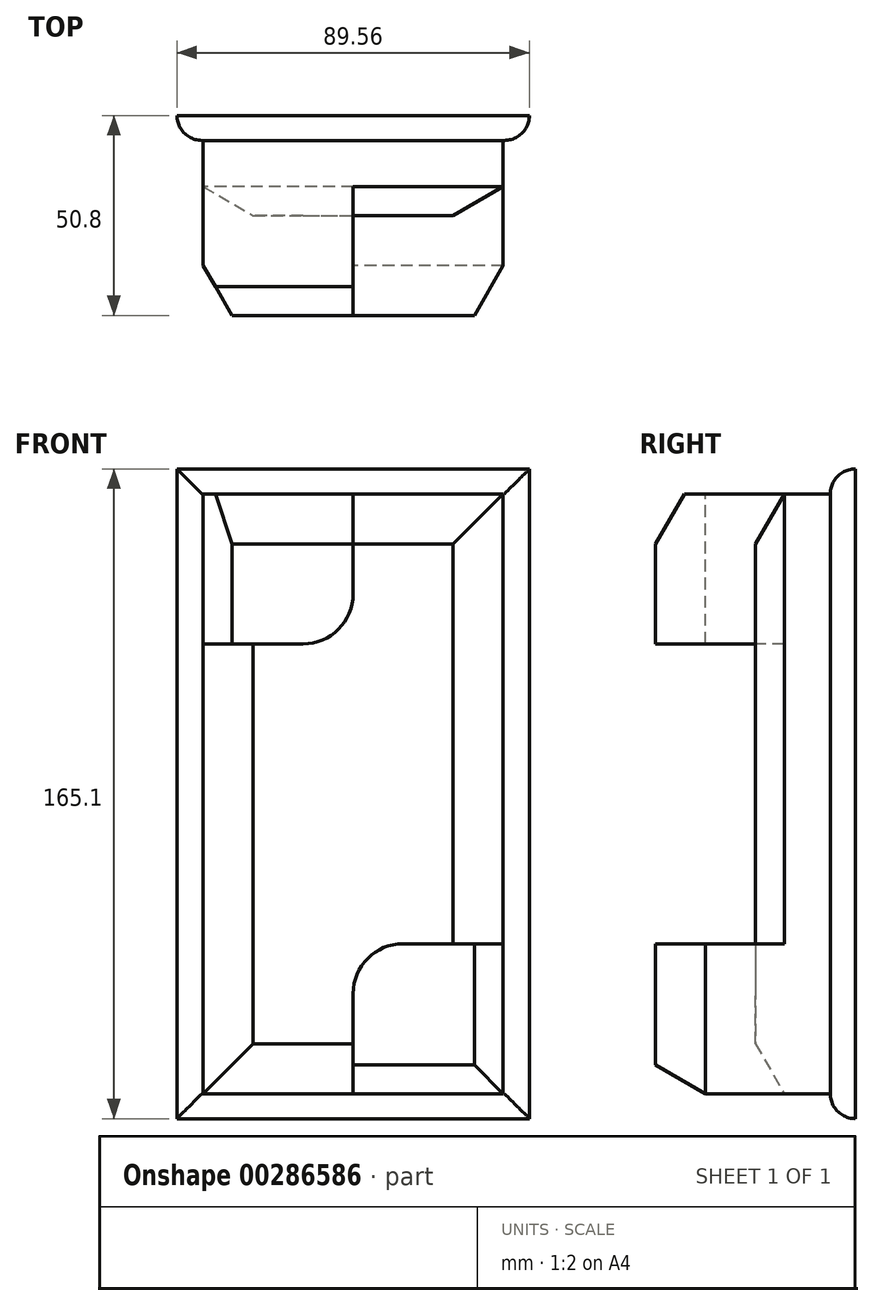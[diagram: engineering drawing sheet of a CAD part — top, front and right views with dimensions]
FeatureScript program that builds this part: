
annotation { "Feature Type Name" : "Feature", "Feature Type Description" : "" }
export const myFeature = defineFeature(function(context is Context, id is Id, definition is map)
    precondition{}
    {
        {
            var Q0;
            Q0=qCreatedBy(makeId("Front.planeOp"),FACE);
            var sketch = newSketch(context, id + "F0", { "sketchPlane" : qUnion([Q0])});
            skLineSegment(sketch, "E0.bottom", {"start": v(-44.78, 82.55) * mm, "end": v(44.78, 82.55) * mm});
            skLineSegment(sketch, "E0.top", {"start": v(-44.78, -82.55) * mm, "end": v(44.78, -82.55) * mm});
            skLineSegment(sketch, "E0.left", {"start": v(-44.78, 82.55) * mm, "end": v(-44.78, -82.55) * mm});
            skLineSegment(sketch, "E0.right", {"start": v(44.78, 82.55) * mm, "end": v(44.78, -82.55) * mm});
            skPoint(sketch, "E0.middle", {"position": v(0, 0) * mm});
            skLineSegment(sketch, "E1.bottom", {"start": v(-38.1, 76.2) * mm, "end": v(38.1, 76.2) * mm});
            skLineSegment(sketch, "E1.top", {"start": v(-38.1, -76.2) * mm, "end": v(38.1, -76.2) * mm});
            skLineSegment(sketch, "E1.left", {"start": v(-38.1, 76.2) * mm, "end": v(-38.1, -76.2) * mm});
            skLineSegment(sketch, "E1.right", {"start": v(38.1, 76.2) * mm, "end": v(38.1, -76.2) * mm});
            skLineSegment(sketch, "E2", {"start": v(0, 76.2) * mm, "end": v(0, 50.8) * mm});
            skPoint(sketch, "E2.endSnap0", {"position": v(0, 76.2) * mm});
            skLineSegment(sketch, "E3", {"start": v(-12.7, 38.1) * mm, "end": v(-38.1, 38.1) * mm});
            skLineSegment(sketch, "E4", {"start": v(0, -76.2) * mm, "end": v(0, -50.8) * mm});
            skPoint(sketch, "E4.endSnap0", {"position": v(0, -76.2) * mm});
            skLineSegment(sketch, "E5", {"start": v(12.7, -38.1) * mm, "end": v(38.1, -38.1) * mm});
            skArc(sketch, "E6", {"start": v(12.7, -38.1) * mm, "mid": v(3.72, -41.82) * mm, "end": v(0, -50.8) * mm});
            skArc(sketch, "E7", {"start": v(-12.7, 38.1) * mm, "mid": v(-3.72, 41.82) * mm, "end": v(0, 50.8) * mm});
            skPoint(sketch, "E8.orphan", {"position": v(0, 38.1) * mm});
            skPoint(sketch, "E9.orphan", {"position": v(0, -38.1) * mm});
            skSolve(sketch);
        }
        {
            var Q0;
            Q0=makeQuery(id+"F0.imprint","IMPRINT",FACE,{"disambiguationData":[TD([[makeQuery(id+"F0.imprint","IMPRINT",EDGE,{"derivedFrom":sQuery(id+"F0.wireOp",EDGE,"E0.bottom")}),-1.0]])]});
            extrude(context, id + "F1", {"entities" : qUnion([Q0]), "depth" : 6.35 * mm});
        }
        {
            var Q0;
            {var subQ9=sQuery(id+"F0.wireOp",EDGE,"E2");Q0=makeQuery(id+"F0.imprint","IMPRINT",FACE,{"disambiguationData":[TD([[makeQuery(id+"F0.imprint","IMPRINT",EDGE,{"derivedFrom":subQ9}),1.0]])]});}
            extrude(context, id + "F2", {"entities" : qUnion([Q0]), "operationType" : NewBodyOperationType.ADD, "depth" : 25.4 * mm});
        }
        {
            var Q0;
            {var subQ0=sQuery(id+"F0.wireOp",EDGE,"E2");Q0=makeQuery(id+"F0.imprint","IMPRINT",FACE,{"disambiguationData":[TD([[makeQuery(id+"F0.imprint","IMPRINT",EDGE,{"derivedFrom":subQ0}),-1.0]])]});}
            var Q1;
            {var subQ1=sQuery(id+"F0.wireOp",EDGE,"E4");Q1=makeQuery(id+"F0.imprint","IMPRINT",FACE,{"disambiguationData":[TD([[makeQuery(id+"F0.imprint","IMPRINT",EDGE,{"derivedFrom":subQ1}),-1.0]])]});}
            extrude(context, id + "F3", {"entities" : qUnion([Q0, Q1]), "operationType" : NewBodyOperationType.ADD, "depth" : 50.8 * mm});
        }
        {
            var Q0;
            Q0=makeQuery(id+"F1.opExtrude","CAP_EDGE",EDGE,{"disambiguationData":[OSD([sQuery(id+"F0.wireOp",EDGE,"E0.left")])],"isStart":false});
            var Q1;
            Q1=makeQuery(id+"F1.opExtrude","CAP_EDGE",EDGE,{"disambiguationData":[OSD([sQuery(id+"F0.wireOp",EDGE,"E0.bottom")])],"isStart":false});
            var Q2;
            Q2=makeQuery(id+"F1.opExtrude","CAP_EDGE",EDGE,{"disambiguationData":[OSD([sQuery(id+"F0.wireOp",EDGE,"E0.top")])],"isStart":false});
            var Q3;
            Q3=makeQuery(id+"F1.opExtrude","CAP_EDGE",EDGE,{"disambiguationData":[OSD([sQuery(id+"F0.wireOp",EDGE,"E0.right")])],"isStart":false});
            fillet(context, id + "F4", {"entities" : qUnion([Q0, Q1, Q2, Q3]), "radius" : 6.35 * mm, "tangentPropagation" : true, "allowEdgeOverflow" : false});
        }
        {
            var Q0;
            Q0=makeQuery(id+"F2.opExtrude","CAP_EDGE",EDGE,{"disambiguationData":[OSD([sQuery(id+"F0.wireOp",EDGE,"E1.top")])],"isStart":false});
            var Q1;
            Q1=makeQuery(id+"F2.opExtrude","CAP_EDGE",EDGE,{"disambiguationData":[OSD([sQuery(id+"F0.wireOp",EDGE,"E1.right")])],"isStart":false});
            var Q2;
            Q2=makeQuery(id+"F2.opExtrude","CAP_EDGE",EDGE,{"disambiguationData":[OSD([sQuery(id+"F0.wireOp",EDGE,"E1.left")])],"isStart":false});
            var Q3;
            Q3=makeQuery(id+"F2.opExtrude","CAP_EDGE",EDGE,{"disambiguationData":[OSD([sQuery(id+"F0.wireOp",EDGE,"E1.bottom")])],"isStart":false});
            chamfer(context, id + "F5", {"entities" : qUnion([Q0, Q1, Q2, Q3]), "chamferType" : ChamferType.OFFSET_ANGLE, "width" : 12.7 * mm, "oppositeDirection" : false, "angle" : 30 * degree, "tangentPropagation" : true});
        }
        {
            var Q0;
            Q0=makeQuery(id+"F3.opExtrude","CAP_EDGE",EDGE,{"disambiguationData":[OSD([sQuery(id+"F0.wireOp",EDGE,"E1.top")])],"isStart":false});
            var Q1;
            Q1=makeQuery(id+"F3.opExtrude","CAP_EDGE",EDGE,{"disambiguationData":[OSD([sQuery(id+"F0.wireOp",EDGE,"E1.right")])],"isStart":false});
            var Q2;
            Q2=makeQuery(id+"F3.opExtrude","CAP_EDGE",EDGE,{"disambiguationData":[OSD([sQuery(id+"F0.wireOp",EDGE,"E1.bottom")])],"isStart":false});
            var Q3;
            Q3=makeQuery(id+"F3.opExtrude","CAP_EDGE",EDGE,{"disambiguationData":[OSD([sQuery(id+"F0.wireOp",EDGE,"E1.left")])],"isStart":false});
            chamfer(context, id + "F6", {"entities" : qUnion([Q0, Q1, Q2, Q3]), "chamferType" : ChamferType.OFFSET_ANGLE, "width" : 12.7 * mm, "oppositeDirection" : true, "angle" : 30 * degree, "tangentPropagation" : true});
        }
    });
